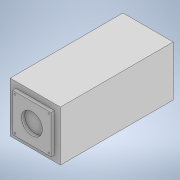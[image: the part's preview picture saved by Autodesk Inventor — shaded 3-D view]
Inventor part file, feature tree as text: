
AUTODESK INVENTOR PART (.ipt)
format: ipt  version: 2022.2 (Build 262287030, 287C)  size: 115,200 bytes
history: native  units: in
note: dims shown in document units (in); Inventor stores cm internally (conversion verified against a paired STEP export)
features: sketch x4, extrude x3, hole x1
ambient origin geometry x8: Origin, YZ Plane, XZ Plane, XY Plane, X Axis, Y Axis, Z Axis, Center Point
bodies: Solid1 (feature_tree)
feature tree (8):
  extrude  "Extrusion1"  Depth=0.8858in
  extrude  "Extrusion2"  Depth=0.6772in
  hole  "Hole2"  [1 undecoded]
  extrude  "Extrusion3"  Depth=0.0591in TaperAngle=0.0deg
  sketch  "Sketch1"  dims[d0=0.8858in d1=0.8858in]
  sketch  "Sketch3"  dims[d2=1.9882in d3=0.0in d13=0.6772in]
  sketch  "Sketch4"  dims[d14=0.6772in d15=0.0591in d16=0.0in]
  sketch  "Sketch5"  dims[d17=0.0276in d18=0.2953in d19=0.1476in d20=0.0984in d21=90.0deg d22=0.0394in d23=0.8108in d24=0.0591in d25=0.0in]
note: 1 required parameter value undecoded (feature->parameter linkage not recoverable at this tier; creation-order binding heuristic only, values carry confidence <= 0.55)
